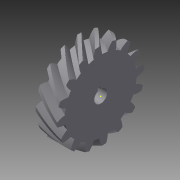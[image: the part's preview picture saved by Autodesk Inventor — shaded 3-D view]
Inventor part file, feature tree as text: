
AUTODESK INVENTOR PART (.ipt)
format: ipt  version: 2015 (Build 190159000, 159)  size: 380,928 bytes
history: native  units: in
note: dims shown in document units (in); Inventor stores cm internally (conversion verified against a paired STEP export)
features: sketch x5, extrude x2, helix x1
ambient origin geometry x8: Origin, YZ Plane, XZ Plane, XY Plane, X Axis, Y Axis, Z Axis, Center Point
bodies: Solid1 (feature_tree)
feature tree (8):
  helix  "Coil1"  [1 undecoded]
  sketch  "Sketch2"  dims[d3=0.1181in d4=1.2008in]
  sketch  "Sketch3"  dims[d5=6.2992in d7=360.0deg]
  extrude  "Extrusion1"  Depth=0.5906in
  extrude  "Extrusion2"  Depth=1.2008in
  sketch  "Sketch1"  dims[d1=0.0591in d2=0.5906in]
  sketch  "Sketch4"  dims[d9=7.874in d10=0.5906in d11=0.3937in d12=0.0in d13=90.0deg d14=90.0deg d15=0.0in d16=0.0in]
  sketch  "Sketch5"  dims[d17=0.3543in d19=0.0394in d20=0.0394in d21=0.0197in d22=0.0787in d23=0.1969in d24=0.0in d25=0.3543in d26=0.5906in d27=0.0in]
note: 1 required parameter value undecoded (feature->parameter linkage not recoverable at this tier; creation-order binding heuristic only, values carry confidence <= 0.55)
